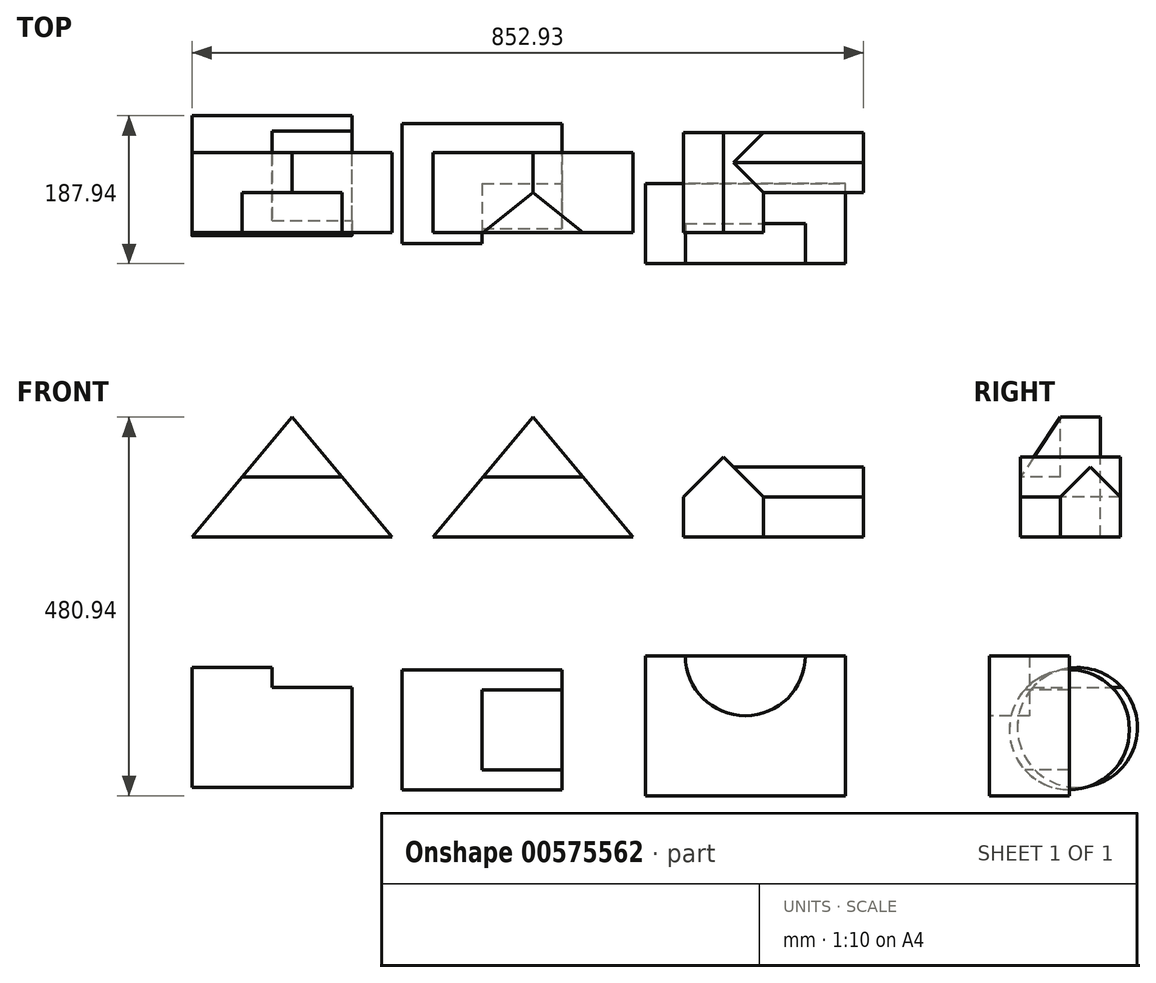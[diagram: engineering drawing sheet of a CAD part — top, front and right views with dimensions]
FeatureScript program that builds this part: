
annotation { "Feature Type Name" : "Feature", "Feature Type Description" : "" }
export const myFeature = defineFeature(function(context is Context, id is Id, definition is map)
    precondition{}
    {
        {
            var Q0;
            Q0=qCreatedBy(makeId("Front.planeOp"),FACE);
            var sketch = newSketch(context, id + "F0", { "sketchPlane" : qUnion([Q0])});
            skLineSegment(sketch, "E0", {"start": v(254, 0) * mm, "end": v(0, 0) * mm});
            skPoint(sketch, "E1", {"position": v(127, 152.4) * mm});
            skLineSegment(sketch, "E2", {"start": v(254, 0) * mm, "end": v(127, 152.4) * mm});
            skLineSegment(sketch, "E3", {"start": v(0, 0) * mm, "end": v(127, 152.4) * mm});
            skPoint(sketch, "E4", {"position": v(63.5, 76.2) * mm});
            skPoint(sketch, "E5", {"position": v(190.5, 76.2) * mm});
            skLineSegment(sketch, "E6", {"start": v(63.5, 76.2) * mm, "end": v(190.5, 76.2) * mm});
            skSolve(sketch);
        }
        {
            var Q0;
            {var subQ3=sQuery(id+"F0.wireOp",EDGE,"E6");Q0=makeQuery(id+"F0.imprint","IMPRINT",FACE,{"disambiguationData":[TD([[makeQuery(id+"F0.imprint","IMPRINT",EDGE,{"derivedFrom":subQ3}),1.0]])]});}
            var Q1;
            {var subQ0=sQuery(id+"F0.wireOp",EDGE,"E0");Q1=makeQuery(id+"F0.imprint","IMPRINT",FACE,{"disambiguationData":[TD([[makeQuery(id+"F0.imprint","IMPRINT",EDGE,{"derivedFrom":subQ0}),-1.0]])]});}
            extrude(context, id + "F1", {"entities" : qUnion([Q0, Q1]), "oppositeDirection" : true, "depth" : 101.6 * mm, "offsetDistance" : 25.4 * mm});
        }
        {
            var Q0;
            Q0=makeQuery(id+"F1.opExtrude","CAP_FACE",FACE,{"disambiguationData":[OSD([sQuery(id+"F0.wireOp",EDGE,"E0"),sQuery(id+"F0.wireOp",EDGE,"E2"),sQuery(id+"F0.wireOp",EDGE,"E3")])],"isStart":true});
            var sketch = newSketch(context, id + "F2", { "sketchPlane" : qUnion([Q0])});
            skLineSegment(sketch, "E7", {"start": v(127, 152.4) * mm, "end": v(127, 76.2) * mm});
            skLineSegment(sketch, "E8", {"start": v(127, 76.2) * mm, "end": v(190.5, 76.2) * mm});
            skLineSegment(sketch, "E9", {"start": v(127, 76.2) * mm, "end": v(63.5, 76.2) * mm});
            skSolve(sketch);
        }
        {
            var Q0;
            {var subQ0=sQuery(id+"F2.wireOp",EDGE,"E7");Q0=makeQuery(id+"F2.imprint","IMPRINT",FACE,{"disambiguationData":[TD([[makeQuery(id+"F2.imprint","IMPRINT",EDGE,{"derivedFrom":subQ0}),-1.0]])]});}
            var Q1;
            {var subQ0=sQuery(id+"F2.wireOp",EDGE,"E7");Q1=makeQuery(id+"F2.imprint","IMPRINT",FACE,{"disambiguationData":[TD([[makeQuery(id+"F2.imprint","IMPRINT",EDGE,{"derivedFrom":subQ0}),1.0]])]});}
            extrude(context, id + "F3", {"entities" : qUnion([Q0, Q1]), "operationType" : NewBodyOperationType.REMOVE, "oppositeDirection" : true, "depth" : 50.8 * mm, "offsetDistance" : 25.4 * mm});
        }
        {
            var Q0;
            Q0=makeQuery(id+"F1.opExtrude","CAP_FACE",FACE,{"disambiguationData":[OSD([sQuery(id+"F0.wireOp",EDGE,"E0"),sQuery(id+"F0.wireOp",EDGE,"E2"),sQuery(id+"F0.wireOp",EDGE,"E3")])],"isStart":true});
            var sketch = newSketch(context, id + "F4", { "sketchPlane" : qUnion([Q0])});
            skLineSegment(sketch, "E10", {"start": v(560.06, 0) * mm, "end": v(306.06, 0) * mm});
            skPoint(sketch, "E11", {"position": v(433.06, 152.4) * mm});
            skLineSegment(sketch, "E12", {"start": v(433.06, 152.4) * mm, "end": v(306.06, 0) * mm});
            skLineSegment(sketch, "E13", {"start": v(560.06, 0) * mm, "end": v(433.06, 152.4) * mm});
            skSolve(sketch);
        }
        {
            var Q0;
            Q0=makeQuery(id+"F4.imprint","IMPRINT",FACE,{"disambiguationData":[TD([[makeQuery(id+"F4.imprint","IMPRINT",EDGE,{"derivedFrom":sQuery(id+"F4.wireOp",EDGE,"E10")}),-1.0]])]});
            extrude(context, id + "F5", {"entities" : qUnion([Q0]), "oppositeDirection" : true, "depth" : 101.6 * mm, "offsetDistance" : 25.4 * mm});
        }
        {
            var Q0;
            Q0=makeQuery(id+"F5.opExtrude","CAP_EDGE",EDGE,{"disambiguationData":[OSD([sQuery(id+"F4.wireOp",EDGE,"E10")])],"isStart":true});
            cPoint(context, id + "F6", {"entities" : qUnion([Q0]), "parameter" : 0.5});
        }
        {
            var Q0;
            Q0=makeQuery(id+"F5.opExtrude","CAP_VERTEX",VERTEX,{"disambiguationData":[OSD([sQuery(id+"F4.wireOp",EDGE,"E12"),sQuery(id+"F4.wireOp",EDGE,"E13")])],"isStart":true});
            var Q1;
            Q1=makeQuery(id+"F5.opExtrude","CAP_VERTEX",VERTEX,{"disambiguationData":[OSD([sQuery(id+"F4.wireOp",EDGE,"E12"),sQuery(id+"F4.wireOp",EDGE,"E13")])],"isStart":false});
            var Q2;
            Q2 = qCreatedBy(id + "F6" ,VERTEX);
            cPlane(context, id + "F7", {"entities" : qUnion([Q0, Q1, Q2]), "cplaneType" : CPlaneType.THREE_POINT, "offset" : 25.4 * mm, "width" : 152.4 * mm, "height" : 152.4 * mm});
        }
        {
            var Q0;
            Q0=qCreatedBy(id+"F7.planeOp",FACE);
            var sketch = newSketch(context, id + "F8", { "sketchPlane" : qUnion([Q0])});
            skLineSegment(sketch, "E14", {"start": v(0, 152.4) * mm, "end": v(0, 76.2) * mm});
            skLineSegment(sketch, "E15", {"start": v(0, 152.4) * mm, "end": v(50.8, 152.4) * mm});
            skLineSegment(sketch, "E16", {"start": v(50.8, 152.4) * mm, "end": v(0, 76.2) * mm});
            skSolve(sketch);
        }
        {
            var Q0;
            Q0 = qSketchRegion(id + "F8", true);
            extrude(context, id + "F9", {"entities" : qUnion([Q0]), "operationType" : NewBodyOperationType.REMOVE, "endBound" : BoundingType.SYMMETRIC, "oppositeDirection" : true, "depth" : 127 * mm, "offsetDistance" : 25.4 * mm});
        }
        {
            var Q0;
            Q0=makeQuery(id+"F5.opExtrude","CAP_FACE",FACE,{"disambiguationData":[OSD([sQuery(id+"F4.wireOp",EDGE,"E10"),sQuery(id+"F4.wireOp",EDGE,"E12"),sQuery(id+"F4.wireOp",EDGE,"E13")])],"isStart":true});
            var sketch = newSketch(context, id + "F10", { "sketchPlane" : qUnion([Q0])});
            skPoint(sketch, "E17", {"position": v(675.13, 101.6) * mm});
            skLineSegment(sketch, "E18", {"start": v(624.33, 50.8) * mm, "end": v(675.13, 101.6) * mm});
            skLineSegment(sketch, "E19", {"start": v(675.13, 101.6) * mm, "end": v(725.93, 50.8) * mm});
            skLineSegment(sketch, "E20", {"start": v(624.33, 0) * mm, "end": v(624.33, 50.8) * mm});
            skLineSegment(sketch, "E21", {"start": v(725.93, 50.8) * mm, "end": v(725.93, 0) * mm});
            skLineSegment(sketch, "E22", {"start": v(624.33, 0) * mm, "end": v(725.93, 0) * mm});
            skSolve(sketch);
        }
        {
            var Q0;
            Q0=makeQuery(id+"F10.imprint","IMPRINT",FACE,{"disambiguationData":[TD([[makeQuery(id+"F10.imprint","IMPRINT",EDGE,{"derivedFrom":sQuery(id+"F10.wireOp",EDGE,"E18")}),-1.0]])]});
            extrude(context, id + "F11", {"entities" : qUnion([Q0]), "oppositeDirection" : true, "depth" : 127 * mm, "offsetDistance" : 25.4 * mm});
        }
        {
            var Q0;
            Q0=makeQuery(id+"F11.opExtrude","SWEPT_FACE",FACE,{"disambiguationData":[OSD([sQuery(id+"F10.wireOp",EDGE,"E21")])]});
            cPlane(context, id + "F12", {"entities" : qUnion([Q0]), "cplaneType" : CPlaneType.OFFSET, "offset" : 127 * mm, "width" : 152.4 * mm, "height" : 152.4 * mm});
        }
        {
            var Q0;
            Q0=qCreatedBy(id+"F12.planeOp",FACE);
            var sketch = newSketch(context, id + "F13", { "sketchPlane" : qUnion([Q0])});
            skLineSegment(sketch, "E23", {"start": v(50.8, 0) * mm, "end": v(50.8, 50.8) * mm});
            skLineSegment(sketch, "E24", {"start": v(50.8, 50.8) * mm, "end": v(88.9, 88.9) * mm});
            skLineSegment(sketch, "E25", {"start": v(88.9, 88.9) * mm, "end": v(127, 50.8) * mm});
            skLineSegment(sketch, "E26", {"start": v(127, 50.8) * mm, "end": v(127, 0) * mm});
            skLineSegment(sketch, "E27", {"start": v(127, 0) * mm, "end": v(50.8, 0) * mm});
            skSolve(sketch);
        }
        {
            var Q0;
            Q0=makeQuery(id+"F13.imprint","IMPRINT",FACE,{"disambiguationData":[TD([[makeQuery(id+"F13.imprint","IMPRINT",EDGE,{"derivedFrom":sQuery(id+"F13.wireOp",EDGE,"E23")}),-1.0]])]});
            extrude(context, id + "F14", {"entities" : qUnion([Q0]), "operationType" : NewBodyOperationType.ADD, "endBound" : BoundingType.UP_TO_NEXT, "oppositeDirection" : true, "depth" : 25.4 * mm, "offsetDistance" : 25.4 * mm});
        }
        {
            var Q0;
            Q0=qCreatedBy(makeId("Right.planeOp"),FACE);
            var sketch = newSketch(context, id + "F15", { "sketchPlane" : qUnion([Q0])});
            skCircle(sketch, "E28", {"center": v(72.25, -241.93) * mm, "radius": 76.2 * mm});
            skSolve(sketch);
        }
        {
            var Q0;
            Q0=makeQuery(id+"F15.imprint","IMPRINT",FACE,{"disambiguationData":[TD([[makeQuery(id+"F15.imprint","IMPRINT",EDGE,{"derivedFrom":sQuery(id+"F15.wireOp",EDGE,"E28")}),1.0]])]});
            extrude(context, id + "F16", {"entities" : qUnion([Q0]), "depth" : 203.2 * mm, "offsetDistance" : 25.4 * mm});
        }
        {
            var Q0;
            Q0=makeQuery(id+"F16.opExtrude","CAP_FACE",FACE,{"disambiguationData":[OSD([sQuery(id+"F15.wireOp",EDGE,"E28")])],"isStart":false});
            var sketch = newSketch(context, id + "F17", { "sketchPlane" : qUnion([Q0])});
            skLineSegment(sketch, "E29", {"start": v(15.45, -191.13) * mm, "end": v(129.05, -191.13) * mm});
            skSolve(sketch);
        }
        {
            var Q0;
            {var subQ0=sQuery(id+"F17.wireOp",EDGE,"E29");Q0=makeQuery(id+"F17.imprint","IMPRINT",FACE,{"disambiguationData":[TD([[makeQuery(id+"F17.imprint","IMPRINT",EDGE,{"derivedFrom":subQ0}),1.0]])]});}
            extrude(context, id + "F18", {"entities" : qUnion([Q0]), "operationType" : NewBodyOperationType.REMOVE, "oppositeDirection" : true, "depth" : 101.6 * mm, "offsetDistance" : 25.4 * mm});
        }
        {
            var Q0;
            Q0=qCreatedBy(makeId("Right.planeOp"),FACE);
            cPlane(context, id + "F19", {"entities" : qUnion([Q0]), "cplaneType" : CPlaneType.OFFSET, "offset" : 266.7 * mm, "width" : 152.4 * mm, "height" : 152.4 * mm});
        }
        {
            var Q0;
            Q0=qCreatedBy(id+"F19.planeOp",FACE);
            var sketch = newSketch(context, id + "F20", { "sketchPlane" : qUnion([Q0])});
            skCircle(sketch, "E30", {"center": v(62.1, -244.63) * mm, "radius": 76.2 * mm});
            skPoint(sketch, "E31", {"position": v(62.1, -168.43) * mm});
            skPoint(sketch, "E32", {"position": v(62.1, -320.83) * mm});
            skPoint(sketch, "E33", {"position": v(138.3, -244.63) * mm});
            skSolve(sketch);
        }
        {
            var Q0;
            Q0=makeQuery(id+"F20.imprint","IMPRINT",FACE,{"disambiguationData":[TD([[makeQuery(id+"F20.imprint","IMPRINT",EDGE,{"derivedFrom":sQuery(id+"F20.wireOp",EDGE,"ULz9lvtC-OSB2-AZkM-0QjZ-vjpLuzNUaG82")}),-1.0]])]});
            var Q1;
            Q1=makeQuery(id+"F20.imprint","IMPRINT",FACE,{"disambiguationData":[TD([[makeQuery(id+"F20.imprint","IMPRINT",EDGE,{"derivedFrom":sQuery(id+"F20.wireOp",EDGE,"E30")}),1.0]])]});
            extrude(context, id + "F21", {"entities" : qUnion([Q0, Q1]), "depth" : 203.2 * mm, "offsetDistance" : 25.4 * mm});
        }
        {
            var Q0;
            Q0=makeQuery(id+"F21.opExtrude","CAP_FACE",FACE,{"disambiguationData":[OSD([sQuery(id+"F20.wireOp",EDGE,"E30")])],"isStart":false});
            var sketch = newSketch(context, id + "F22", { "sketchPlane" : qUnion([Q0])});
            skPoint(sketch, "E34", {"position": v(62.1, -244.63) * mm});
            skLineSegment(sketch, "E35", {"start": v(62.1, -295.43) * mm, "end": v(62.1, -244.63) * mm});
            skLineSegment(sketch, "E36", {"start": v(62.1, -295.43) * mm, "end": v(5.31, -295.43) * mm});
            skLineSegment(sketch, "E37", {"start": v(62.1, -244.63) * mm, "end": v(62.1, -193.83) * mm});
            skLineSegment(sketch, "E38", {"start": v(62.1, -193.83) * mm, "end": v(5.31, -193.83) * mm});
            skSolve(sketch);
        }
        {
            var Q0;
            Q0=makeQuery(id+"F22.imprint","IMPRINT",FACE,{"disambiguationData":[TD([[makeQuery(id+"F22.imprint","IMPRINT",EDGE,{"derivedFrom":sQuery(id+"F22.wireOp",EDGE,"E35")}),1.0]])]});
            extrude(context, id + "F23", {"entities" : qUnion([Q0]), "operationType" : NewBodyOperationType.REMOVE, "oppositeDirection" : true, "depth" : 101.6 * mm, "offsetDistance" : 25.4 * mm});
        }
        {
            var Q0;
            Q0=makeQuery(id+"F23.boolean.opBoolean","COPY",FACE,{"derivedFrom":makeQuery(id+"F23.opExtrude","SWEPT_FACE",FACE,{"disambiguationData":[OSD([sQuery(id+"F22.wireOp",EDGE,"E35"),sQuery(id+"F22.wireOp",EDGE,"E37")])]})});
            var sketch = newSketch(context, id + "F24", { "sketchPlane" : qUnion([Q0])});
            skLineSegment(sketch, "E39", {"start": v(575.89, -328.54) * mm, "end": v(575.89, -150.74) * mm});
            skLineSegment(sketch, "E40", {"start": v(575.89, -150.74) * mm, "end": v(829.89, -150.74) * mm});
            skLineSegment(sketch, "E41", {"start": v(829.89, -150.74) * mm, "end": v(829.89, -328.54) * mm});
            skLineSegment(sketch, "E42", {"start": v(829.89, -328.54) * mm, "end": v(575.89, -328.54) * mm});
            skSolve(sketch);
        }
        {
            var Q0;
            Q0=makeQuery(id+"F24.imprint","IMPRINT",FACE,{"disambiguationData":[TD([[makeQuery(id+"F24.imprint","IMPRINT",EDGE,{"derivedFrom":sQuery(id+"F24.wireOp",EDGE,"E39")}),-1.0]])]});
            extrude(context, id + "F25", {"entities" : qUnion([Q0]), "depth" : 101.6 * mm, "offsetDistance" : 25.4 * mm});
        }
        {
            var Q0;
            Q0=makeQuery(id+"F25.opExtrude","CAP_FACE",FACE,{"disambiguationData":[OSD([sQuery(id+"F24.wireOp",EDGE,"E39"),sQuery(id+"F24.wireOp",EDGE,"E40"),sQuery(id+"F24.wireOp",EDGE,"E41"),sQuery(id+"F24.wireOp",EDGE,"E42")])],"isStart":false});
            var sketch = newSketch(context, id + "F26", { "sketchPlane" : qUnion([Q0])});
            skArc(sketch, "E43", {"start": v(626.69, -150.74) * mm, "mid": v(702.89, -226.94) * mm, "end": v(779.09, -150.74) * mm});
            skSolve(sketch);
        }
        {
            var Q0;
            {var subQ0=sQuery(id+"F26.wireOp",EDGE,"E43");Q0=makeQuery(id+"F26.imprint","IMPRINT",FACE,{"disambiguationData":[TD([[makeQuery(id+"F26.imprint","IMPRINT",EDGE,{"derivedFrom":subQ0}),1.0]])]});}
            extrude(context, id + "F27", {"entities" : qUnion([Q0]), "operationType" : NewBodyOperationType.REMOVE, "oppositeDirection" : true, "depth" : 50.8 * mm, "offsetDistance" : 25.4 * mm});
        }
    });
